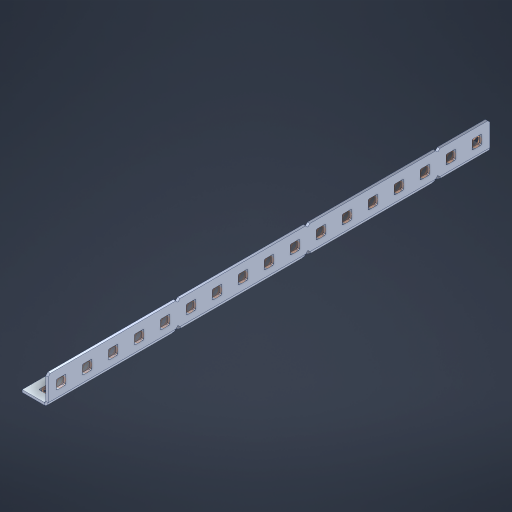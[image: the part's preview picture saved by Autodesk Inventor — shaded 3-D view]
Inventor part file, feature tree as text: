
AUTODESK INVENTOR PART (.ipt)
format: ipt  version: 2023 (Build 270158000, 158)  size: 692,736 bytes
history: native  units: in
note: dims shown in document units (in); Inventor stores cm internally (conversion verified against a paired STEP export)
features: other x39, extrude x33, sheet_metal_op x10, sketch x8, mirror x1, pattern_linear x1, chamfer x1
ambient origin geometry x8: Origin, YZ Plane, XZ Plane, XY Plane, X Axis, Y Axis, Z Axis, Center Point
bodies: Solid1 (feature_tree), Body (feature_tree)
feature tree (93):
  other  "Flange Pattern Plane"
  sheet_metal_op  "Flange Pattern"
  sheet_metal_op  "Body Pattern"
  other  "Arc Length"
  mirror  "Notch Mirror"
  pattern_linear  "Notch Pattern"  Spacing1=0.1875in  [1 undecoded]
  chamfer  "End Chamfer"
  extrude  "Half Cut"  Depth=0.0469in
  sketch  "Sketch1"  dims[d0=2.5in]
  other  "Plate1"
  sketch  "Sketch2"  dims[d1=8.5in]
  other  "Plate2"
  sheet_metal_op  "Bend1"
  sheet_metal_op  "Corner1"
  sketch  "Sketch3"  dims[d2=0.0469in]
  other  "Flange Pattern Sketch"
  sketch  "Sketch7"  dims[d3=0.0469in]
  other  "Srf1"
  other  "Srf2"
  sketch  "Sketch8"  dims[d4=0.0234in]
  sketch  "Sketch9"  dims[d5=0.0938in]
  other  "Srf91"
  sheet_metal_op  "Body Pattern Sketch"
  other  "Srf92"
  sketch  "Sketch13"  dims[d6=0.0469in]
  sketch  "Sketch14"  dims[d7=0.5in d8=90.0deg d9=0.0312in d10=0.1875in d11=0.0469in d12=0.0469in d16=0.182in d17=0.02in d18=0.0469in d19=0.0in d20=0.25in d21=0.25in d46=0.172in d47=1.0in d48=0.0in d49=0.182in d50=0.02in d51=0.25in d52=0.25in d53=0.0469in d54=0.0in d55=0.172in d56=1.0in d57=0.0in d60=6.6929in d62=0.5in d63=0.3937in d65=0.5in d85=0.1227in d86=0.1659in d88=0.04in d89=0.0469in d90=0.0in d91=0.04in d92=0.0491in d95=2.5in d96=0.04in d97=0.25in d98=45.0deg d101=0.0in d102=2.497in d131=0.5in d132=6.6929in d134=0.5in d139=0.5in]
  other  "Srf856"
  other  "Srf1310"
  other  "Srf1311"
  other  "Srf1312"
  other  "Srf1376"
  other  "Srf1377"
  other  "Srf1728"
  other  "Srf1755"
  other  "Srf1878"
  other  "Srf1879"
  other  "Srf1880"
  other  "Srf1881"
  other  "Srf1882"
  other  "Srf1883"
  other  "Srf1884"
  other  "Srf1885"
  other  "Srf1886"
  other  "Srf1887"
  other  "Srf1888"
  other  "Srf1942"
  other  "Srf1943"
  other  "Srf1944"
  other  "Srf1945"
  other  "Srf1946"
  other  "Srf1947"
  other  "Srf1948"
  other  "Srf1949"
  other  "Srf1950"
  other  "Srf1951"
  other  "Srf1952"
  sheet_metal_op  "Flange Stamp"
  sheet_metal_op  "Flange Circle"
  sheet_metal_op  "Body Stamp"
  sheet_metal_op  "Body Circle"
  sheet_metal_op  "Notch"
  extrude  "ExtrusionSrf2"  Depth=0.0469in
  extrude  "ExtrusionSrf92"  Depth=0.5in
  extrude  "ExtrusionSrf856"  Depth=0.02in
  extrude  "ExtrusionSrf1310"  Depth=0.0469in
  extrude  "ExtrusionSrf1311"  TaperAngle=0.0deg  [1 undecoded]
  extrude  "ExtrusionSrf1312"  Depth=0.5in
  extrude  "ExtrusionSrf1376"  Depth=0.5in
  extrude  "ExtrusionSrf1377"  Depth=0.5in
  extrude  "ExtrusionSrf1728"  Depth=0.5in TaperAngle=0.0deg
  extrude  "ExtrusionSrf1755"  Depth=0.5in
  extrude  "ExtrusionSrf1878"  Depth=0.02in
  extrude  "ExtrusionSrf1879"  Depth=0.5in
  extrude  "ExtrusionSrf1880"  Depth=0.5in
  extrude  "ExtrusionSrf1881"  Depth=0.0469in
  extrude  "ExtrusionSrf1882"  TaperAngle=0.0deg  [1 undecoded]
  extrude  "ExtrusionSrf1883"  Depth=0.5in
  extrude  "ExtrusionSrf1884"  Depth=0.5in TaperAngle=0.0deg
  extrude  "ExtrusionSrf1885"  Depth=0.5in
  extrude  "ExtrusionSrf1886"  Depth=0.5in
  extrude  "ExtrusionSrf1887"  Depth=0.5in
  extrude  "ExtrusionSrf1888"  Depth=0.5in
  extrude  "ExtrusionSrf1942"  Depth=0.5in
  extrude  "ExtrusionSrf1943"  Depth=0.0469in
  extrude  "ExtrusionSrf1944"  TaperAngle=0.0deg  [1 undecoded]
  extrude  "ExtrusionSrf1945"  Depth=0.5in
  extrude  "ExtrusionSrf1946"  Depth=0.5in
  extrude  "ExtrusionSrf1947"  Depth=0.5in
  extrude  "ExtrusionSrf1948"  Depth=0.5in TaperAngle=45.0deg
  extrude  "ExtrusionSrf1949"  TaperAngle=0.0deg  [1 undecoded]
  extrude  "ExtrusionSrf1950"  Depth=0.5in
  extrude  "ExtrusionSrf1951"  Depth=0.5in
  extrude  "ExtrusionSrf1952"  Depth=0.5in
note: 5 required parameter values undecoded (feature->parameter linkage not recoverable at this tier; creation-order binding heuristic only, values carry confidence <= 0.55)
